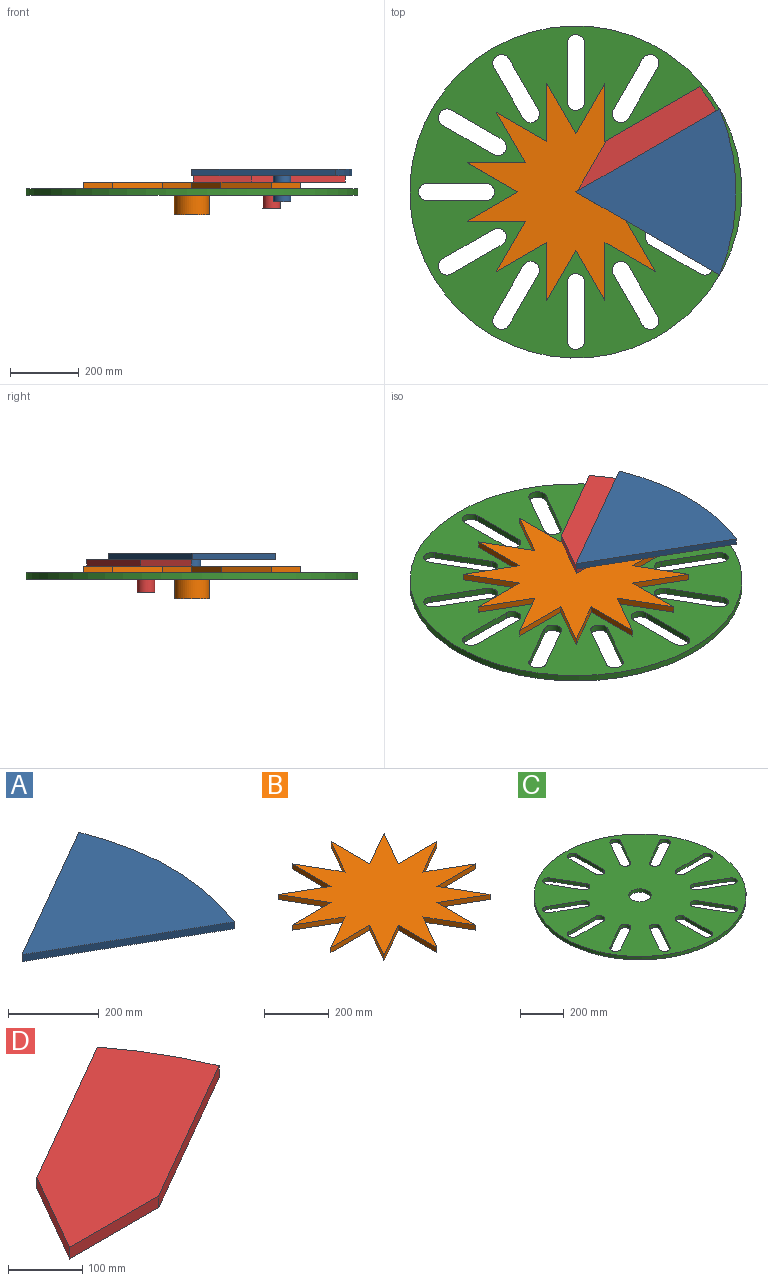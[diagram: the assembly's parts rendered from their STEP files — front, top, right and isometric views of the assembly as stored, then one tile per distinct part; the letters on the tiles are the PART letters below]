
ASSEMBLY  parts=4 mates=3
PART A: 7 faces, bbox 465.6x482.6x95.3 mm
  f0: plane 417.94x241.3mm, normal (-0.5,0.87,0), area 9193.5mm2, adj f1,f2,f3,f4
  f1: plane 417.94x241.3mm, normal (-0.5,-0.87,0), area 9193.5mm2, adj f0,f2,f3,f4
  f2: cylinder r=635mm len=482.6mm, axis (0,0,-1), area 9430.5mm2, adj f0,f1,f3,f4
  f3: plane 482.6x465.58mm, normal (0,0,1), area 116293.9mm2, adj f0,f1,f2
  f4: plane 482.6x465.58mm, normal (0,0,-1), area 114267.1mm2, adj f0,f1,f2,f5
  f5: cylinder r=25.4mm len=76.2mm, axis (0,0,1), area 12161mm2, adj f4,f6
  f6: plane 50.8x50.8mm, normal (0,0,-1), area 2026.8mm2, adj f5
PART B: 28 faces, bbox 632.3x632.3x95.3 mm
  f0: plane 146.72x84.71mm, normal (0.5,0.87,0), area 3227.5mm2, adj f1,f23,f24,f25
  f1: plane 146.72x84.71mm, normal (0.5,-0.87,0), area 3227.5mm2, adj f0,f2,f24,f25
  f2: plane 169.42x19.05mm, normal (0,1,0), area 3227.5mm2, adj f1,f3,f24,f25
  f3: plane 146.72x84.71mm, normal (0.87,-0.5,0), area 3227.5mm2, adj f2,f4,f24,f25
  f4: plane 146.72x84.71mm, normal (-0.5,0.87,0), area 3227.5mm2, adj f3,f5,f24,f25
  f5: plane 169.42x19.05mm, normal (1,0,0), area 3227.5mm2, adj f4,f6,f24,f25
  f6: plane 146.72x84.71mm, normal (-0.87,0.5,0), area 3227.5mm2, adj f5,f7,f24,f25
  f7: plane 146.72x84.71mm, normal (0.87,0.5,0), area 3227.5mm2, adj f6,f8,f24,f25
  f8: plane 169.42x19.05mm, normal (-1,0,0), area 3227.5mm2, adj f7,f9,f24,f25
  f9: plane 146.72x84.71mm, normal (0.5,0.87,0), area 3227.5mm2, adj f8,f10,f24,f25
  f10: plane 146.72x84.71mm, normal (-0.87,-0.5,0), area 3227.5mm2, adj f9,f11,f24,f25
  f11: plane 169.42x19.05mm, normal (0,1,0), area 3227.5mm2, adj f10,f12,f24,f25
  f12: plane 146.72x84.71mm, normal (-0.5,-0.87,0), area 3227.5mm2, adj f11,f13,f24,f25
  f13: plane 146.72x84.71mm, normal (-0.5,0.87,0), area 3227.5mm2, adj f12,f14,f24,f25
  f14: plane 169.42x19.05mm, normal (0,-1,0), area 3227.5mm2, adj f13,f15,f24,f25
  f15: plane 146.72x84.71mm, normal (-0.87,0.5,0), area 3227.5mm2, adj f14,f16,f24,f25
  f16: plane 146.72x84.71mm, normal (0.5,-0.87,0), area 3227.5mm2, adj f15,f17,f24,f25
  f17: plane 169.42x19.05mm, normal (-1,0,0), area 3227.5mm2, adj f16,f18,f24,f25
  f18: plane 146.72x84.71mm, normal (0.87,-0.5,0), area 3227.5mm2, adj f17,f19,f24,f25
  f19: plane 146.72x84.71mm, normal (-0.87,-0.5,0), area 3227.5mm2, adj f18,f20,f24,f25
  f20: plane 169.42x19.05mm, normal (1,0,0), area 3227.5mm2, adj f19,f21,f24,f25
  f21: plane 146.72x84.71mm, normal (-0.5,-0.87,0), area 3227.5mm2, adj f20,f22,f24,f25
  f22: plane 146.72x84.71mm, normal (0.87,0.5,0), area 3227.5mm2, adj f21,f23,f24,f25
  f23: plane 169.42x19.05mm, normal (0,-1,0), area 3227.5mm2, adj f0,f22,f24,f25
  f24: plane 632.29x632.29mm, normal (0,0,1), area 172224mm2, adj f0,f1,f2,f3,f4,f5,f6,f7
  f25: plane 632.29x632.29mm, normal (0,0,-1), area 164116.7mm2, adj f0,f1,f2,f3,f4,f5,f6,f7
  f26: cylinder r=50.8mm len=101.6mm, axis (0,0,1), area 24322mm2, adj f25,f27
  f27: plane 101.6x101.6mm, normal (0,0,-1), area 8107.3mm2, adj f26
PART C: 52 faces, bbox 965.2x965.2x19.1 mm
  f0: cylinder r=25.4mm len=47.4mm, axis (0,0,1), area 1520.1mm2, adj f1,f49,f50,f51
  f1: plane 146.72x84.71mm, normal (-0.5,0.87,0), area 3227.5mm2, adj f0,f2,f50,f51
  f2: cylinder r=25.4mm len=47.4mm, axis (0,0,1), area 1520.1mm2, adj f1,f49,f50,f51
  f3: cylinder r=25.4mm len=47.4mm, axis (0,0,1), area 1520.1mm2, adj f4,f36,f50,f51
  f4: plane 146.72x84.71mm, normal (-0.87,0.5,0), area 3227.5mm2, adj f3,f5,f50,f51
  f5: cylinder r=25.4mm len=47.4mm, axis (0,0,1), area 1520.1mm2, adj f4,f36,f50,f51
  f6: cylinder r=25.4mm len=50.8mm, axis (0,0,1), area 1520.1mm2, adj f7,f37,f50,f51
  f7: plane 169.42x19.05mm, normal (-1,0,0), area 3227.5mm2, adj f6,f8,f50,f51
  f8: cylinder r=25.4mm len=50.8mm, axis (0,0,1), area 1520.1mm2, adj f7,f37,f50,f51
  f9: cylinder r=25.4mm len=47.4mm, axis (0,0,1), area 1520.1mm2, adj f10,f38,f50,f51
  f10: plane 146.72x84.71mm, normal (-0.87,-0.5,0), area 3227.5mm2, adj f9,f11,f50,f51
  f11: cylinder r=25.4mm len=47.4mm, axis (0,0,1), area 1520.1mm2, adj f10,f38,f50,f51
  f12: cylinder r=25.4mm len=47.4mm, axis (0,0,1), area 1520.1mm2, adj f13,f39,f50,f51
  f13: plane 146.72x84.71mm, normal (-0.5,-0.87,0), area 3227.5mm2, adj f12,f14,f50,f51
  f14: cylinder r=25.4mm len=47.4mm, axis (0,0,1), area 1520.1mm2, adj f13,f39,f50,f51
  f15: cylinder r=25.4mm len=50.8mm, axis (0,0,1), area 1520.1mm2, adj f16,f40,f50,f51
  f16: plane 169.42x19.05mm, normal (0,-1,0), area 3227.5mm2, adj f15,f17,f50,f51
  f17: cylinder r=25.4mm len=50.8mm, axis (0,0,1), area 1520.1mm2, adj f16,f40,f50,f51
  f18: cylinder r=25.4mm len=47.4mm, axis (0,0,1), area 1520.1mm2, adj f19,f41,f50,f51
  f19: plane 146.72x84.71mm, normal (0.5,-0.87,0), area 3227.5mm2, adj f18,f20,f50,f51
  f20: cylinder r=25.4mm len=47.4mm, axis (0,0,1), area 1520.1mm2, adj f19,f41,f50,f51
  f21: cylinder r=25.4mm len=47.4mm, axis (0,0,1), area 1520.1mm2, adj f22,f42,f50,f51
  f22: plane 146.72x84.71mm, normal (0.87,-0.5,0), area 3227.5mm2, adj f21,f23,f50,f51
  f23: cylinder r=25.4mm len=47.4mm, axis (0,0,1), area 1520.1mm2, adj f22,f42,f50,f51
  f24: cylinder r=25.4mm len=50.8mm, axis (0,0,1), area 1520.1mm2, adj f25,f43,f50,f51
  f25: plane 169.42x19.05mm, normal (1,0,0), area 3227.5mm2, adj f24,f26,f50,f51
  f26: cylinder r=25.4mm len=50.8mm, axis (0,0,1), area 1520.1mm2, adj f25,f43,f50,f51
  f27: cylinder r=25.4mm len=47.4mm, axis (0,0,1), area 1520.1mm2, adj f28,f44,f50,f51
  f28: plane 146.72x84.71mm, normal (0.87,0.5,0), area 3227.5mm2, adj f27,f29,f50,f51
  f29: cylinder r=25.4mm len=47.4mm, axis (0,0,1), area 1520.1mm2, adj f28,f44,f50,f51
  f30: cylinder r=25.4mm len=47.4mm, axis (0,0,1), area 1520.1mm2, adj f31,f45,f50,f51
  f31: plane 146.72x84.71mm, normal (0.5,0.87,0), area 3227.5mm2, adj f30,f32,f50,f51
  f32: cylinder r=25.4mm len=47.4mm, axis (0,0,1), area 1520.1mm2, adj f31,f45,f50,f51
  f33: cylinder r=25.4mm len=50.8mm, axis (0,0,1), area 1520.1mm2, adj f34,f48,f50,f51
  f34: plane 169.42x19.05mm, normal (0,1,0), area 3227.5mm2, adj f33,f35,f50,f51
  f35: cylinder r=25.4mm len=50.8mm, axis (0,0,1), area 1520.1mm2, adj f34,f48,f50,f51
  f36: plane 146.72x84.71mm, normal (0.87,-0.5,0), area 3227.5mm2, adj f3,f5,f50,f51
  f37: plane 169.42x19.05mm, normal (1,0,0), area 3227.5mm2, adj f6,f8,f50,f51
  f38: plane 146.72x84.71mm, normal (0.87,0.5,0), area 3227.5mm2, adj f9,f11,f50,f51
  f39: plane 146.72x84.71mm, normal (0.5,0.87,0), area 3227.5mm2, adj f12,f14,f50,f51
  f40: plane 169.42x19.05mm, normal (0,1,0), area 3227.5mm2, adj f15,f17,f50,f51
  f41: plane 146.72x84.71mm, normal (-0.5,0.87,0), area 3227.5mm2, adj f18,f20,f50,f51
  f42: plane 146.72x84.71mm, normal (-0.87,0.5,0), area 3227.5mm2, adj f21,f23,f50,f51
  f43: plane 169.42x19.05mm, normal (-1,0,0), area 3227.5mm2, adj f24,f26,f50,f51
  f44: plane 146.72x84.71mm, normal (-0.87,-0.5,0), area 3227.5mm2, adj f27,f29,f50,f51
  f45: plane 146.72x84.71mm, normal (-0.5,-0.87,0), area 3227.5mm2, adj f30,f32,f50,f51
  f46: cylinder r=482.6mm len=965.2mm, axis (0,0,1), area 57764.7mm2, adj f50,f51
  f47: cylinder r=50.8mm len=101.6mm, axis (0,0,1), area 6080.5mm2, adj f50,f51
  f48: plane 169.42x19.05mm, normal (0,-1,0), area 3227.5mm2, adj f33,f35,f50,f51
  f49: plane 146.72x84.71mm, normal (0.5,-0.87,0), area 3227.5mm2, adj f0,f2,f50,f51
  f50: plane 965.2x965.2mm, normal (0,0,-1), area 595976.3mm2, adj f0,f1,f2,f3,f4,f5,f6,f7
  f51: plane 965.2x965.2mm, normal (0,0,1), area 595976.3mm2, adj f0,f1,f2,f3,f4,f5,f6,f7
PART D: 9 faces, bbox 440.6x303.3x95.3 mm
  f0: plane 271.22x156.59mm, normal (0.5,-0.87,0), area 5966mm2, adj f1,f4,f5,f6
  f1: cylinder r=635mm len=146.72mm, axis (0,0,-1), area 3237.2mm2, adj f0,f2,f5,f6
  f2: plane 271.22x156.59mm, normal (-0.5,0.87,0), area 5966mm2, adj f1,f3,f5,f6
  f3: plane 146.72x84.71mm, normal (-0.87,0.5,0), area 3227.5mm2, adj f2,f4,f5,f6
  f4: plane 169.42x19.05mm, normal (0,-1,0), area 3227.5mm2, adj f0,f3,f5,f6
  f5: plane 440.64x303.31mm, normal (0,0,1), area 66130.2mm2, adj f0,f1,f2,f3,f4
  f6: plane 440.64x303.31mm, normal (0,0,-1), area 64103.3mm2, adj f0,f1,f2,f3,f4,f7
  f7: cylinder r=25.4mm len=76.2mm, axis (0,0,1), area 12161mm2, adj f6,f8
  f8: plane 50.8x50.8mm, normal (0,0,-1), area 2026.8mm2, adj f7
PLACE A t=(-176.32,13.78,69.18)mm
PLACE B t=(-6.9,13.78,31.08)mm
PLACE C t=(-6.9,13.78,31.08)mm
PLACE D t=(-149.09,-68.31,50.13)mm
MATE parallel A.f5 <-> C.f35  axis (0,0,-1) through (255.48,13.78,69.18)mm
MATE parallel D.f7 <-> C.f2  axis (0,0,-1) through (224.86,147.59,50.13)mm
MATE cylindrical C.f47 <-> B.f26  axis (0,0,1) through (-6.9,13.78,31.08)mm
